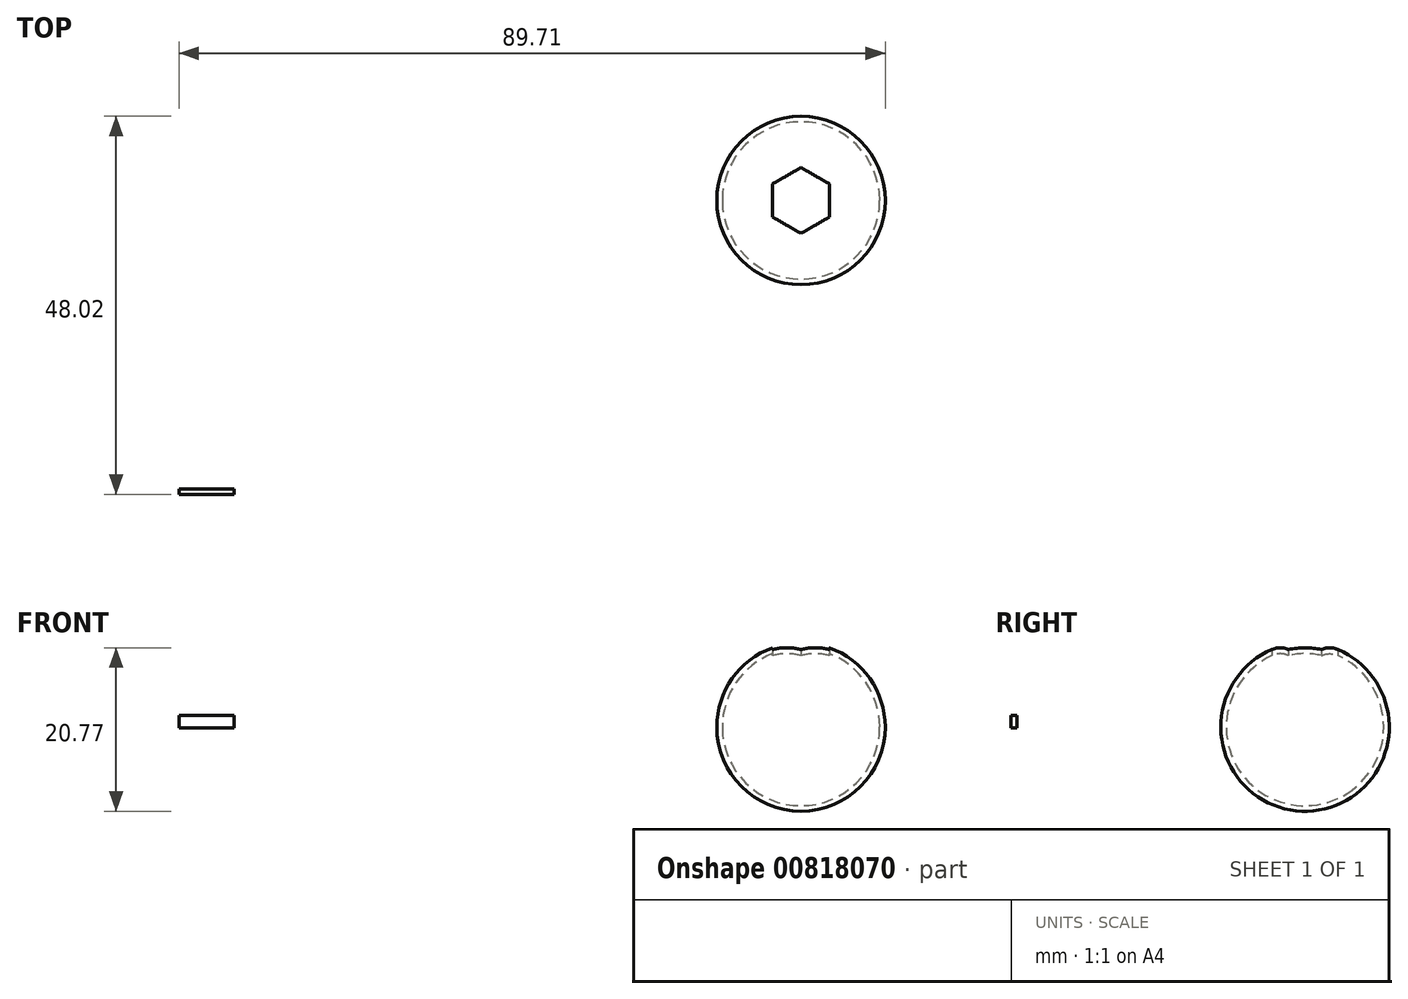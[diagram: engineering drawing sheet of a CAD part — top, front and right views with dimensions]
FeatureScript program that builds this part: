
annotation { "Feature Type Name" : "Feature", "Feature Type Description" : "" }
export const myFeature = defineFeature(function(context is Context, id is Id, definition is map)
    precondition{}
    {
        {
            var Q0;
            Q0=qCreatedBy(makeId("Top.planeOp"),FACE);
            var sketch = newSketch(context, id + "F0", { "sketchPlane" : qUnion([Q0])});
            skArc(sketch, "E0", {"start": v(10, 0) * mm, "mid": v(0, 10) * mm, "end": v(-10, 0) * mm});
            skArc(sketch, "E1.0", {"start": v(10.7, 0) * mm, "mid": v(0, 10.7) * mm, "end": v(-10.7, 0) * mm});
            skLineSegment(sketch, "E2", {"start": v(10, 0) * mm, "end": v(10.7, 0) * mm});
            skLineSegment(sketch, "E3", {"start": v(-10.7, 0) * mm, "end": v(-10, 0) * mm});
            skCircle(sketch, "E4.cCircle", {"center": v(0, 0) * mm, "radius": 3.62 * mm, "construction": true});
            skLineSegment(sketch, "E4.0", {"start": v(3.62, 2.1) * mm, "end": v(3.62, -2.1) * mm});
            skLineSegment(sketch, "E4.1", {"start": v(3.62, -2.1) * mm, "end": v(0, -4.19) * mm});
            skLineSegment(sketch, "E4.2", {"start": v(0, -4.19) * mm, "end": v(-3.63, -2.1) * mm});
            skLineSegment(sketch, "E4.3", {"start": v(-3.62, -2.1) * mm, "end": v(-3.62, 2.1) * mm});
            skLineSegment(sketch, "E4.4", {"start": v(-3.63, 2.1) * mm, "end": v(0, 4.19) * mm});
            skLineSegment(sketch, "E4.5", {"start": v(0, 4.19) * mm, "end": v(3.62, 2.1) * mm});
            skPoint(sketch, "E4.0.midPoint", {"position": v(3.62, 0) * mm});
            skSolve(sketch);
        }
        {
            var Q0;
            Q0=makeQuery(id+"F0.imprint","IMPRINT",FACE,{"disambiguationData":[TD([[makeQuery(id+"F0.imprint","IMPRINT",EDGE,{"derivedFrom":sQuery(id+"F0.wireOp",EDGE,"E4.0")}),-1.0]])]});
            var sketch = newSketch(context, id + "F1", { "sketchPlane" : qUnion([Q0])});
            skLineSegment(sketch, "E5.0.0", {"start": v(3.62, 2.1) * mm, "end": v(0, 4.19) * mm});
            skLineSegment(sketch, "E5.0.1", {"start": v(0, 4.19) * mm, "end": v(-3.63, 2.1) * mm});
            skLineSegment(sketch, "E5.0.2", {"start": v(-3.62, 2.1) * mm, "end": v(-3.62, -2.1) * mm});
            skLineSegment(sketch, "E5.0.3", {"start": v(-3.63, -2.1) * mm, "end": v(0, -4.19) * mm});
            skLineSegment(sketch, "E5.0.4", {"start": v(0, -4.19) * mm, "end": v(3.62, -2.1) * mm});
            skLineSegment(sketch, "E5.0.5", {"start": v(3.62, -2.1) * mm, "end": v(3.62, 2.1) * mm});
            skSolve(sketch);
        }
        {
            var Q0;
            Q0=makeQuery(id+"F0.imprint","IMPRINT",FACE,{"disambiguationData":[TD([[makeQuery(id+"F0.imprint","IMPRINT",EDGE,{"derivedFrom":sQuery(id+"F0.wireOp",EDGE,"E0")}),-1.0]])]});
            var Q1;
            Q1=sQuery(id+"F0.wireOp",EDGE,"E3");
            revolve(context, id + "F2", {"surfaceOperationType" : NewSurfaceOperationType.NEW, "entities" : qUnion([Q0]), "axis" : qUnion([Q1]), "revolveType" : RevolveType.FULL});
        }
        {
            var Q0;
            Q0 = qSketchRegion(id + "F1", true);
            extrude(context, id + "F3", {"entities" : qUnion([Q0]), "operationType" : NewBodyOperationType.REMOVE, "depth" : 25 * mm, "offsetDistance" : 25 * mm});
        }
        {
            var Q0;
            Q0=qCreatedBy(makeId("Top.planeOp"),FACE);
            var sketch = newSketch(context, id + "F4", { "sketchPlane" : qUnion([Q0])});
            skLineSegment(sketch, "E6.bottom", {"start": v(-79.01, -36.62) * mm, "end": v(-72.01, -36.62) * mm});
            skLineSegment(sketch, "E6.top", {"start": v(-79.01, -37.32) * mm, "end": v(-72.01, -37.32) * mm});
            skLineSegment(sketch, "E6.left", {"start": v(-79.01, -36.62) * mm, "end": v(-79.01, -37.32) * mm});
            skLineSegment(sketch, "E6.right", {"start": v(-72.01, -36.62) * mm, "end": v(-72.01, -37.32) * mm});
            skSolve(sketch);
        }
        {
            var Q0;
            Q0 = qSketchRegion(id + "F4", true);
            extrude(context, id + "F5", {"entities" : qUnion([Q0]), "depth" : 1.5 * mm, "offsetDistance" : 25 * mm, "hasSecondDirection" : true, "secondDirectionOppositeDirection" : true, "secondDirectionDepth" : .1 * mm});
        }
    });
